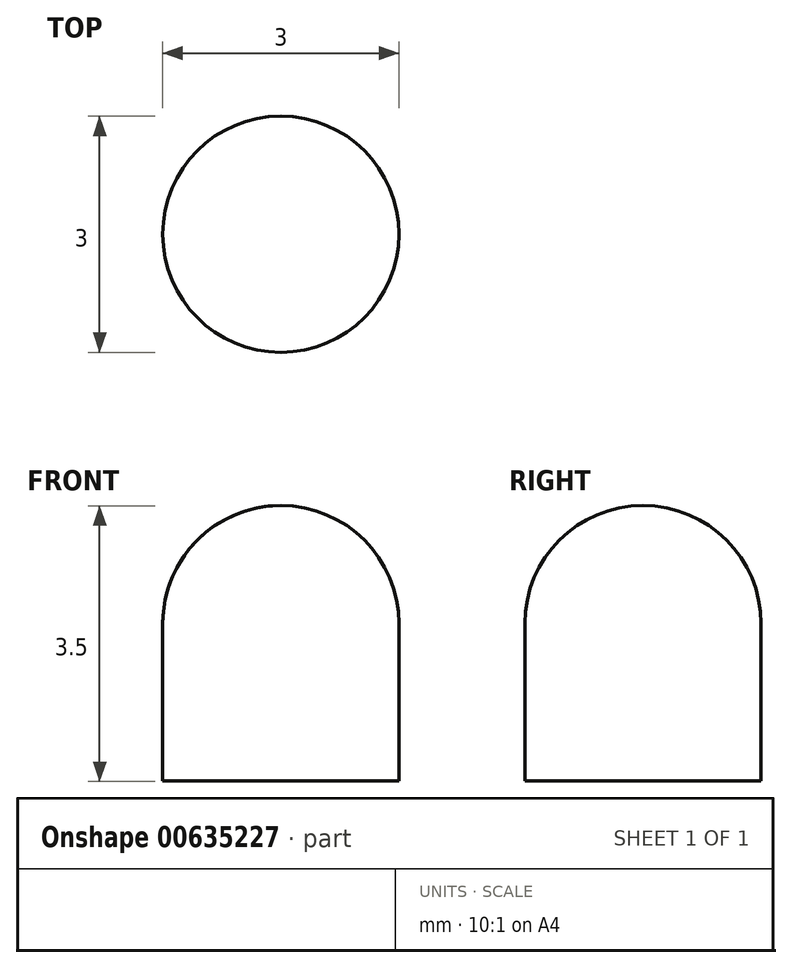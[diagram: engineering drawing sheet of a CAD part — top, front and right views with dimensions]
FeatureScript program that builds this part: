
annotation { "Feature Type Name" : "Feature", "Feature Type Description" : "" }
export const myFeature = defineFeature(function(context is Context, id is Id, definition is map)
    precondition{}
    {
        {
            var Q0;
            Q0=qCreatedBy(makeId("Front.planeOp"),FACE);
            var sketch = newSketch(context, id + "F0", { "sketchPlane" : qUnion([Q0])});
            skLineSegment(sketch, "E0", {"start": v(0, 49.28) * mm, "end": v(0, -52.68) * mm, "construction": true});
            skLineSegment(sketch, "E1", {"start": v(-1.5, -1.15) * mm, "end": v(-1.5, 0.85) * mm});
            skArc(sketch, "E2", {"start": v(0, 2.35) * mm, "mid": v(-1.06, 1.91) * mm, "end": v(-1.5, 0.85) * mm});
            skLineSegment(sketch, "E3", {"start": v(-1.5, -1.15) * mm, "end": v(0, -1.15) * mm});
            skLineSegment(sketch, "E4", {"start": v(0, -1.15) * mm, "end": v(0, 2.35) * mm});
            skSolve(sketch);
        }
        {
            var Q0;
            Q0 = qSketchRegion(id + "F0", true);
            var Q1;
            Q1=sQuery(id+"F0.wireOp",EDGE,"E0");
            revolve(context, id + "F1", {"entities" : qUnion([Q0]), "axis" : qUnion([Q1]), "revolveType" : RevolveType.FULL});
        }
    });
